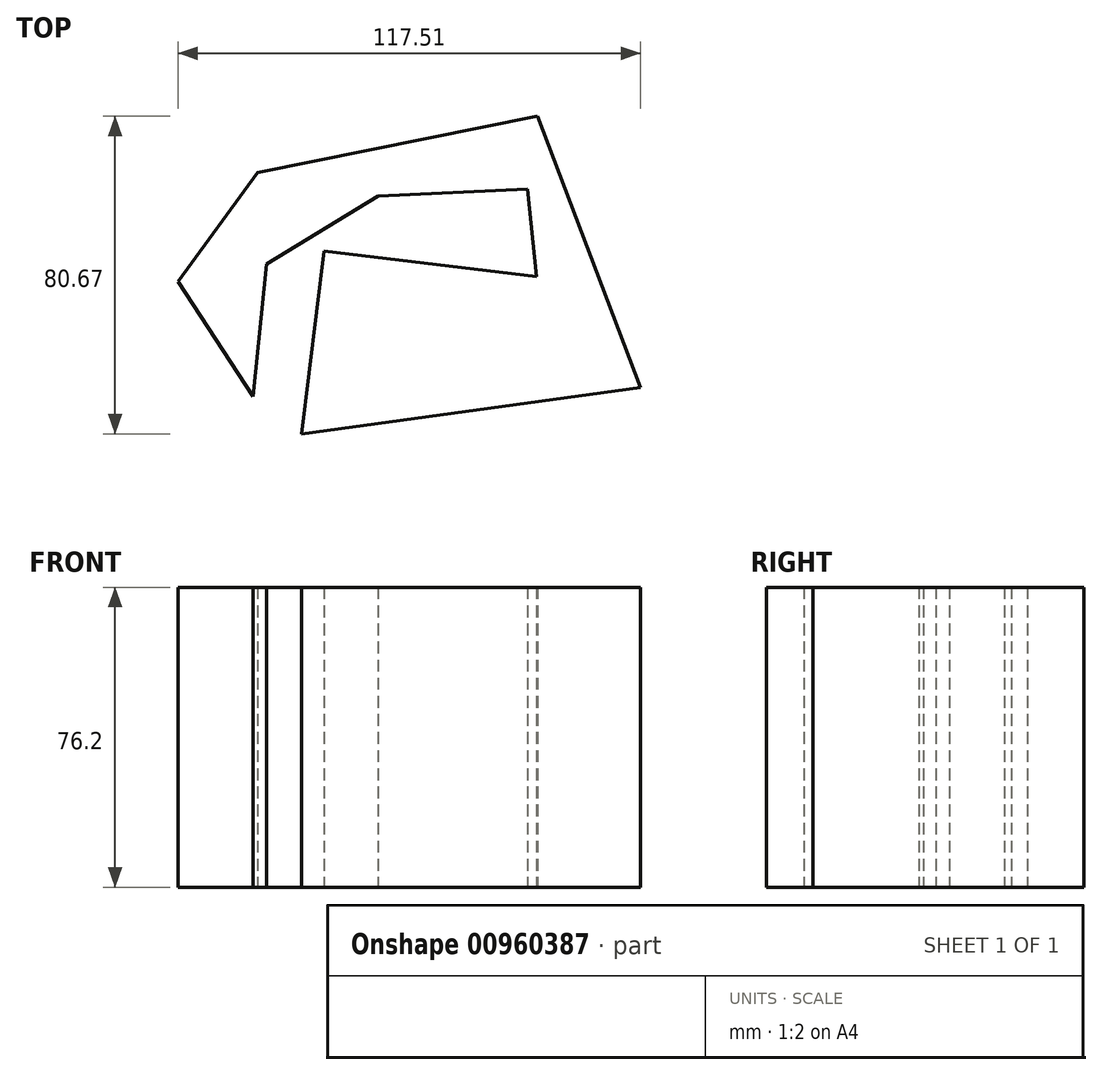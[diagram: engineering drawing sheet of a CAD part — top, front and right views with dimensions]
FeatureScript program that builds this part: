
annotation { "Feature Type Name" : "Feature", "Feature Type Description" : "" }
export const myFeature = defineFeature(function(context is Context, id is Id, definition is map)
    precondition{}
    {
        {
            var Q0;
            Q0=qCreatedBy(makeId("Top.planeOp"),FACE);
            var sketch = newSketch(context, id + "F0", { "sketchPlane" : qUnion([Q0])});
            skLineSegment(sketch, "E0", {"start": v(-45.67, 38.68) * mm, "end": v(25.36, 53.04) * mm});
            skLineSegment(sketch, "E1", {"start": v(25.36, 53.04) * mm, "end": v(51.62, -15.92) * mm});
            skLineSegment(sketch, "E2", {"start": v(51.62, -15.92) * mm, "end": v(-34.53, -27.63) * mm});
            skLineSegment(sketch, "E3", {"start": v(-34.53, -27.63) * mm, "end": v(-28.86, 18.85) * mm});
            skLineSegment(sketch, "E4", {"start": v(-28.86, 18.85) * mm, "end": v(25.1, 12.26) * mm});
            skLineSegment(sketch, "E5", {"start": v(25.1, 12.26) * mm, "end": v(22.9, 34.53) * mm});
            skLineSegment(sketch, "E6", {"start": v(22.9, 34.53) * mm, "end": v(-15.07, 32.83) * mm});
            skLineSegment(sketch, "E7", {"start": v(-15.07, 32.83) * mm, "end": v(-43.4, 15.44) * mm});
            skLineSegment(sketch, "E8", {"start": v(-43.4, 15.44) * mm, "end": v(-46.8, -18.18) * mm});
            skLineSegment(sketch, "E9", {"start": v(-46.8, -18.18) * mm, "end": v(-65.89, 11.1) * mm});
            skLineSegment(sketch, "E10", {"start": v(-65.89, 11.1) * mm, "end": v(-45.67, 38.68) * mm});
            skSolve(sketch);
        }
        {
            var Q0;
            Q0=makeQuery(id+"F0.imprint","IMPRINT",FACE,{"disambiguationData":[TD([[makeQuery(id+"F0.imprint","IMPRINT",EDGE,{"derivedFrom":sQuery(id+"F0.wireOp",EDGE,"E0")}),-1.0]])]});
            extrude(context, id + "F1", {"entities" : qUnion([Q0]), "depth" : 76.2 * mm, "offsetDistance" : 25.4 * mm});
        }
    });
